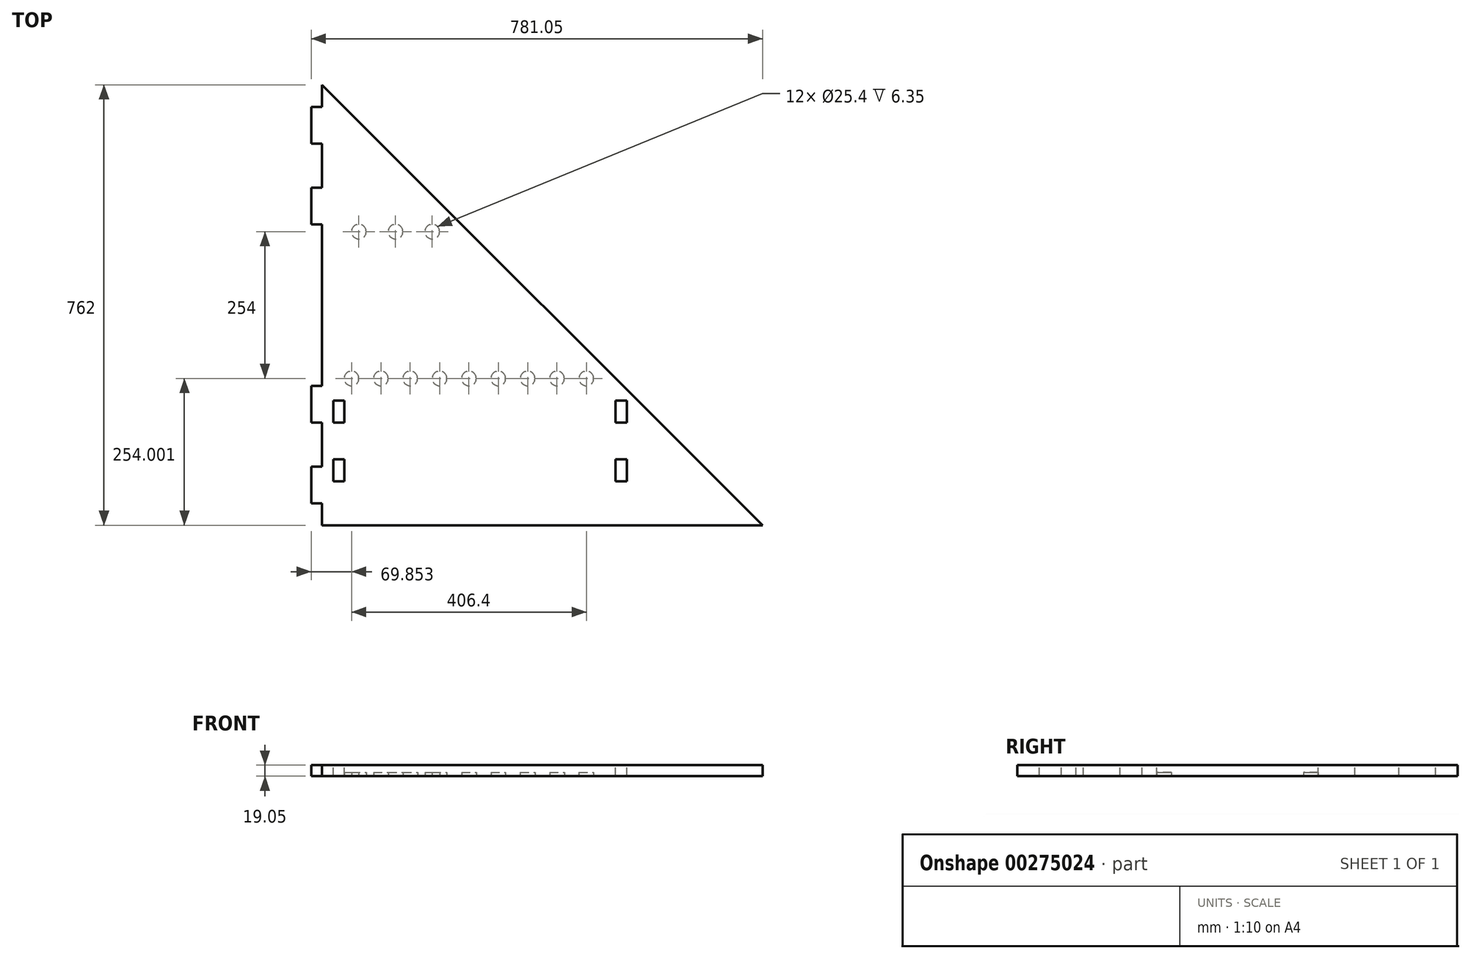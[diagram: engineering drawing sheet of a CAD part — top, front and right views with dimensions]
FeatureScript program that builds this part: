
annotation { "Feature Type Name" : "Feature", "Feature Type Description" : "" }
export const myFeature = defineFeature(function(context is Context, id is Id, definition is map)
    precondition{}
    {
        {
            var Q0;
            Q0=qCreatedBy(makeId("Top.planeOp"),FACE);
            var sketch = newSketch(context, id + "F0", { "sketchPlane" : qUnion([Q0])});
            skLineSegment(sketch, "E0", {"start": v(-486.35, -377.57) * mm, "end": v(275.65, -377.57) * mm});
            skLineSegment(sketch, "E1", {"start": v(-486.35, -377.57) * mm, "end": v(-486.35, 384.43) * mm});
            skLineSegment(sketch, "E2", {"start": v(-486.35, 384.43) * mm, "end": v(275.65, -377.57) * mm});
            skSolve(sketch);
        }
        {
            var Q0;
            Q0 = qSketchRegion(id + "F0", true);
            extrude(context, id + "F1", {"entities" : qUnion([Q0]), "depth" : 19.05 * mm});
        }
        {
            var Q0;
            Q0=makeQuery(id+"F1.opExtrude","CAP_FACE",FACE,{"disambiguationData":[OSD([sQuery(id+"F0.wireOp",EDGE,"E0"),sQuery(id+"F0.wireOp",EDGE,"E1"),sQuery(id+"F0.wireOp",EDGE,"E2")])],"isStart":true});
            var sketch = newSketch(context, id + "F2", { "sketchPlane" : qUnion([Q0])});
            skLineSegment(sketch, "E3", {"start": v(-486.35, 123.57) * mm, "end": v(21.65, 123.57) * mm});
            skLineSegment(sketch, "E4", {"start": v(-232.35, -130.43) * mm, "end": v(-486.35, -130.43) * mm});
            skCircle(sketch, "E5", {"center": v(-295.85, -130.43) * mm, "radius": 12.7 * mm});
            skCircle(sketch, "E6", {"center": v(-359.35, -130.43) * mm, "radius": 12.7 * mm});
            skCircle(sketch, "E7", {"center": v(-422.85, -130.43) * mm, "radius": 12.7 * mm});
            skCircle(sketch, "E8", {"center": v(-29.15, 123.57) * mm, "radius": 12.7 * mm});
            skCircle(sketch, "E9", {"center": v(-79.95, 123.57) * mm, "radius": 12.7 * mm});
            skCircle(sketch, "E10", {"center": v(-130.75, 123.57) * mm, "radius": 12.7 * mm});
            skCircle(sketch, "E11", {"center": v(-181.55, 123.57) * mm, "radius": 12.7 * mm});
            skCircle(sketch, "E12", {"center": v(-232.35, 123.57) * mm, "radius": 12.7 * mm});
            skCircle(sketch, "E13", {"center": v(-283.15, 123.57) * mm, "radius": 12.7 * mm});
            skCircle(sketch, "E14", {"center": v(-333.95, 123.57) * mm, "radius": 12.7 * mm});
            skCircle(sketch, "E15", {"center": v(-384.75, 123.57) * mm, "radius": 12.7 * mm});
            skCircle(sketch, "E16", {"center": v(-435.55, 123.57) * mm, "radius": 12.7 * mm});
            skSolve(sketch);
        }
        {
            var Q0;
            Q0 = qSketchRegion(id + "F2", true);
            extrude(context, id + "F3", {"entities" : qUnion([Q0]), "operationType" : NewBodyOperationType.REMOVE, "oppositeDirection" : true, "depth" : 6.35 * mm});
        }
        {
            var Q0;
            Q0=makeQuery(id+"F1.opExtrude","CAP_FACE",FACE,{"disambiguationData":[OSD([sQuery(id+"F0.wireOp",EDGE,"E0"),sQuery(id+"F0.wireOp",EDGE,"E1"),sQuery(id+"F0.wireOp",EDGE,"E2")])],"isStart":false});
            var sketch = newSketch(context, id + "F4", { "sketchPlane" : qUnion([Q0])});
            skLineSegment(sketch, "E17", {"start": v(-486.35, -377.57) * mm, "end": v(-486.35, -104.52) * mm, "construction": true});
            skLineSegment(sketch, "E18.bottom", {"start": v(-467.3, -263.27) * mm, "end": v(-448.25, -263.27) * mm});
            skLineSegment(sketch, "E18.top", {"start": v(-467.3, -301.37) * mm, "end": v(-448.25, -301.37) * mm});
            skLineSegment(sketch, "E18.left", {"start": v(-467.3, -263.27) * mm, "end": v(-467.3, -301.37) * mm});
            skLineSegment(sketch, "E18.right", {"start": v(-448.25, -263.27) * mm, "end": v(-448.25, -301.37) * mm});
            skPoint(sketch, "E19.oppositeSnap0", {"position": v(-448.25, -282.32) * mm});
            skLineSegment(sketch, "E19.bottom", {"start": v(-467.3, -161.67) * mm, "end": v(-448.25, -161.67) * mm});
            skLineSegment(sketch, "E19.top", {"start": v(-467.3, -199.77) * mm, "end": v(-448.25, -199.77) * mm});
            skLineSegment(sketch, "E19.left", {"start": v(-467.3, -161.67) * mm, "end": v(-467.3, -199.77) * mm});
            skLineSegment(sketch, "E19.right", {"start": v(-448.25, -161.67) * mm, "end": v(-448.25, -199.77) * mm});
            skLineSegment(sketch, "E20.bottom", {"start": v(40.7, -263.27) * mm, "end": v(21.65, -263.27) * mm});
            skLineSegment(sketch, "E20.top", {"start": v(40.7, -301.37) * mm, "end": v(21.65, -301.37) * mm});
            skLineSegment(sketch, "E20.left", {"start": v(40.7, -263.27) * mm, "end": v(40.7, -301.37) * mm});
            skLineSegment(sketch, "E20.right", {"start": v(21.65, -263.27) * mm, "end": v(21.65, -301.37) * mm});
            skLineSegment(sketch, "E21.bottom", {"start": v(21.65, -199.77) * mm, "end": v(40.7, -199.77) * mm});
            skLineSegment(sketch, "E21.top", {"start": v(21.65, -161.67) * mm, "end": v(40.7, -161.67) * mm});
            skLineSegment(sketch, "E21.left", {"start": v(21.65, -199.77) * mm, "end": v(21.65, -161.67) * mm});
            skLineSegment(sketch, "E21.right", {"start": v(40.7, -199.77) * mm, "end": v(40.7, -161.67) * mm});
            skSolve(sketch);
        }
        {
            var Q0;
            Q0 = qSketchRegion(id + "F4", true);
            extrude(context, id + "F5", {"entities" : qUnion([Q0]), "operationType" : NewBodyOperationType.REMOVE, "oppositeDirection" : true, "depth" : 25.4 * mm});
        }
        {
            var Q0;
            Q0=makeQuery(id+"F1.opExtrude","SWEPT_FACE",FACE,{"disambiguationData":[OSD([sQuery(id+"F0.wireOp",EDGE,"E1")])]});
            var sketch = newSketch(context, id + "F6", { "sketchPlane" : qUnion([Q0])});
            skLineSegment(sketch, "E22", {"start": v(-384.43, 0) * mm, "end": v(0, 0) * mm});
            skLineSegment(sketch, "E23", {"start": v(0, 0) * mm, "end": v(377.57, 0) * mm});
            skLineSegment(sketch, "E24.bottom", {"start": v(-346.33, 0) * mm, "end": v(-282.83, 0) * mm});
            skLineSegment(sketch, "E24.top", {"start": v(-346.33, 19.05) * mm, "end": v(-282.83, 19.05) * mm});
            skLineSegment(sketch, "E24.left", {"start": v(-346.33, 0) * mm, "end": v(-346.33, 19.05) * mm});
            skLineSegment(sketch, "E24.right", {"start": v(-282.83, 0) * mm, "end": v(-282.83, 19.05) * mm});
            skLineSegment(sketch, "E25.bottom", {"start": v(-206.63, 0) * mm, "end": v(-143.13, 0) * mm});
            skLineSegment(sketch, "E25.top", {"start": v(-206.63, 19.05) * mm, "end": v(-143.13, 19.05) * mm});
            skLineSegment(sketch, "E25.left", {"start": v(-206.63, 0) * mm, "end": v(-206.63, 19.05) * mm});
            skLineSegment(sketch, "E25.right", {"start": v(-143.13, 0) * mm, "end": v(-143.13, 19.05) * mm});
            skLineSegment(sketch, "E26.bottom", {"start": v(339.47, 0) * mm, "end": v(275.97, 0) * mm});
            skLineSegment(sketch, "E26.top", {"start": v(339.47, 19.05) * mm, "end": v(275.97, 19.05) * mm});
            skLineSegment(sketch, "E26.left", {"start": v(339.47, 0) * mm, "end": v(339.47, 19.05) * mm});
            skLineSegment(sketch, "E26.right", {"start": v(275.97, 0) * mm, "end": v(275.97, 19.05) * mm});
            skLineSegment(sketch, "E27.bottom", {"start": v(199.77, 0) * mm, "end": v(136.27, 0) * mm});
            skLineSegment(sketch, "E27.top", {"start": v(199.77, 19.05) * mm, "end": v(136.27, 19.05) * mm});
            skLineSegment(sketch, "E27.left", {"start": v(199.77, 0) * mm, "end": v(199.77, 19.05) * mm});
            skLineSegment(sketch, "E27.right", {"start": v(136.27, 0) * mm, "end": v(136.27, 19.05) * mm});
            skLineSegment(sketch, "E28", {"start": v(-384.43, 0) * mm, "end": v(377.57, 0) * mm});
            skSolve(sketch);
        }
        {
            var Q0;
            Q0 = qSketchRegion(id + "F6", true);
            extrude(context, id + "F7", {"entities" : qUnion([Q0]), "operationType" : NewBodyOperationType.ADD, "depth" : 19.05 * mm, "offsetDistance" : 25.4 * mm});
        }
    });
